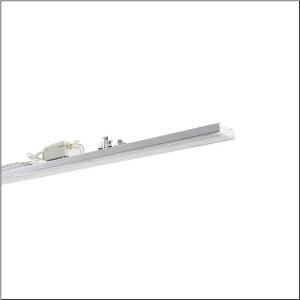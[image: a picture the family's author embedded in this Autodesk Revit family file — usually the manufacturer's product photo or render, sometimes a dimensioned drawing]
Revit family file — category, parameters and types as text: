
# Revit family: licross_r__21_recessed_mo_52tl12dv4fxgd_e48e
name_source: partatom
category: Lighting Fixtures
units: mm (PartAtom-declared; Revit-internal decimal feet)

## family parameters
Cut with Voids When Loaded = No
Host = Face
Light Source = No
Part Type = Normal
Room Calculation Point = No
Round Connector Dimension = Use Diameter
Shared = No

## types (1)
- --- (1 x LED, 15420 lm, 85.3 W, 4000K)
    Apparent Load = 85 VA
    CIE Flux Codes = 72 92 99 100 100
    Color Rendering = 80
    Color Temperature = 4000K
    Default Elevation = 1800 mm
    Description = Licross® 21 Recessed MO, luminaire insert, of sheet steel, galvanised, coil coated, white, length: 2.250mm, width: 66mm, height: 67mm, LED rated luminous flux: 15.420lm, light colour: 840, control gear: DALI 2, with plug, 6-pole, with phase selection, mains connection: 220..240V, AC/DC, 0/50..60Hz, rated input power: 85W, without changeover relay, for emergency light function, for central battery installations according to DIN EN 60598-2-22, halogen-free wiring, primary optical cover: cover, of PMMA, light emission: direct distribution, primary light characteristic: symmetric, protection rating (complete): IP40, insulation class (complete): insulation class I (protective earthing), certification: CE, ENEC, VDE, UKCA, protection symbol: D if used in an environment without relevant dust loads with corresponding accessories, impact resistance: IK06, permissible ambient temperature for indoor applications: -25..+35°C, standard: EN 60598-2-22, corresponds to IFS (International Featured Standards) requirements for safety and quality in the food industry, reducing of maximum allowable ambient temperature of 5°C with ceiling mounting, LABS conformity tested according to VDMA 24364:2018-05, packaging unit: 1 piece
    Height = 58 mm
    Lamp = 1 x LED
    Lamp Light Flux = 15420 lm
    Lamp Power = 85.3 W
    Lamp count = 1
    Length = 2250 mm
    Luminous efficacy = 181 lm/W
    Manufacturer = Siteco
    ModVariant = No
    Model = 52TL12DV4FXGD
    Mounting Place = Ceiling
    Mounting Type = Pendant
    Number of Poles = 1
    OnlyDefault = Yes
    Power Factor = 1
    Product Name = Licross® 21 Recessed MO
    Product group = luminaire insert
    ProductGroupID = 901
    Protection Class = Protection class I
    Protection Degree = IP 40
    RLX_Detail_Level = 1
    RLX_Emergency_Light_Flux = 0 lm
    RLX_Emergency_Type = 0
    RLX_Emergency_Type_DB = No
    RlxData = <blob elided: 30073 chars, md5=e01bbd99>
    Socket = socket
    Standby Power = 0 W
    System Light Flux = 15420 lm
    System Power = 85 W
    Type Comments = : AC-mode, luminous flux: 100 % | dim-lin: 254 | 390 mA
    Type Image = l_1296930.jpg
    URL = http://relux.com
    VarID = @adj_043143
    Voltage = 0 V
    Weight = 0.00 kg
    Width = 66 mm

## geometry (parser evidence)
native form markers: Blend x4, Sweep x9
no freeform markers — native parametric forms only
